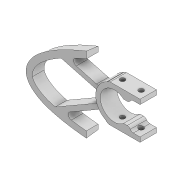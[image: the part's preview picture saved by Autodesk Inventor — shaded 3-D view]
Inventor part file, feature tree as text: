
AUTODESK INVENTOR PART (.ipt)
format: ipt  version: 2022 (Build 260153000, 153)  size: 547,840 bytes
history: native  units: mm
features: extrude x6, sketch x6, projected_geometry x3, shell x1, fillet x1, thicken_offset x1, chamfer x1
ambient origin geometry x8: Origin, YZ Plane, XZ Plane, XY Plane, X Axis, Y Axis, Z Axis, Center Point
bodies: Solid1 (feature_tree)
feature tree (19):
  extrude  "Extrusion1"  Depth=2.0mm
  shell  "Shell1"  Thickness=38.0mm
  extrude  "Extrusion9"  Depth=12.0mm
  fillet  "Fillet2"  Radius=2.0mm
  extrude  "Extrusion10"  Depth=11.0mm
  extrude  "Extrusion12"  TaperAngle=30.0deg  [1 undecoded]
  thicken_offset  "Thicken1"
  chamfer  "Chamfer1"  Distance=2.0mm
  extrude  "Extrusion13"  Depth=1.0mm
  extrude  "Extrusion14"  Depth=1.5mm
  sketch  "Sketch3"  dims[d0=5.0mm d1=0.0mm d2=2.0mm d68=38.0mm]
  sketch  "Sketch25"  dims[d69=8.05mm d70=12.0mm d71=2.0mm]
  projected_geometry  "Projected Loop13"
  sketch  "Sketch26"  dims[d72=11.0mm d73=11.0mm]
  sketch  "Sketch28"  dims[d74=15.0deg d75=30.0deg]
  sketch  "Sketch29"  dims[d76=2.0mm]
  projected_geometry  "Projected Loop14"
  sketch  "Sketch30"  dims[d77=1.0mm d79=2.0mm d80=1.0mm d81=1.5mm d82=1.5mm d83=5.0mm d84=0.0mm d85=3.0mm d86=3.0mm d87=1.5mm d88=25.0mm d89=25.0mm d90=100.0mm d91=0.0mm d98=2.1mm d99=2.5mm d100=20.0mm d101=0.0mm d102=2.1mm d103=3.0mm d104=0.7mm d105=1.0mm d106=5.0mm d107=0.65mm d108=45.0deg d109=1.0mm d110=0.0mm d111=1.0mm d112=0.0mm]
  projected_geometry  "Projected Loop15"
note: 1 required parameter value undecoded (feature->parameter linkage not recoverable at this tier; creation-order binding heuristic only, values carry confidence <= 0.55)
